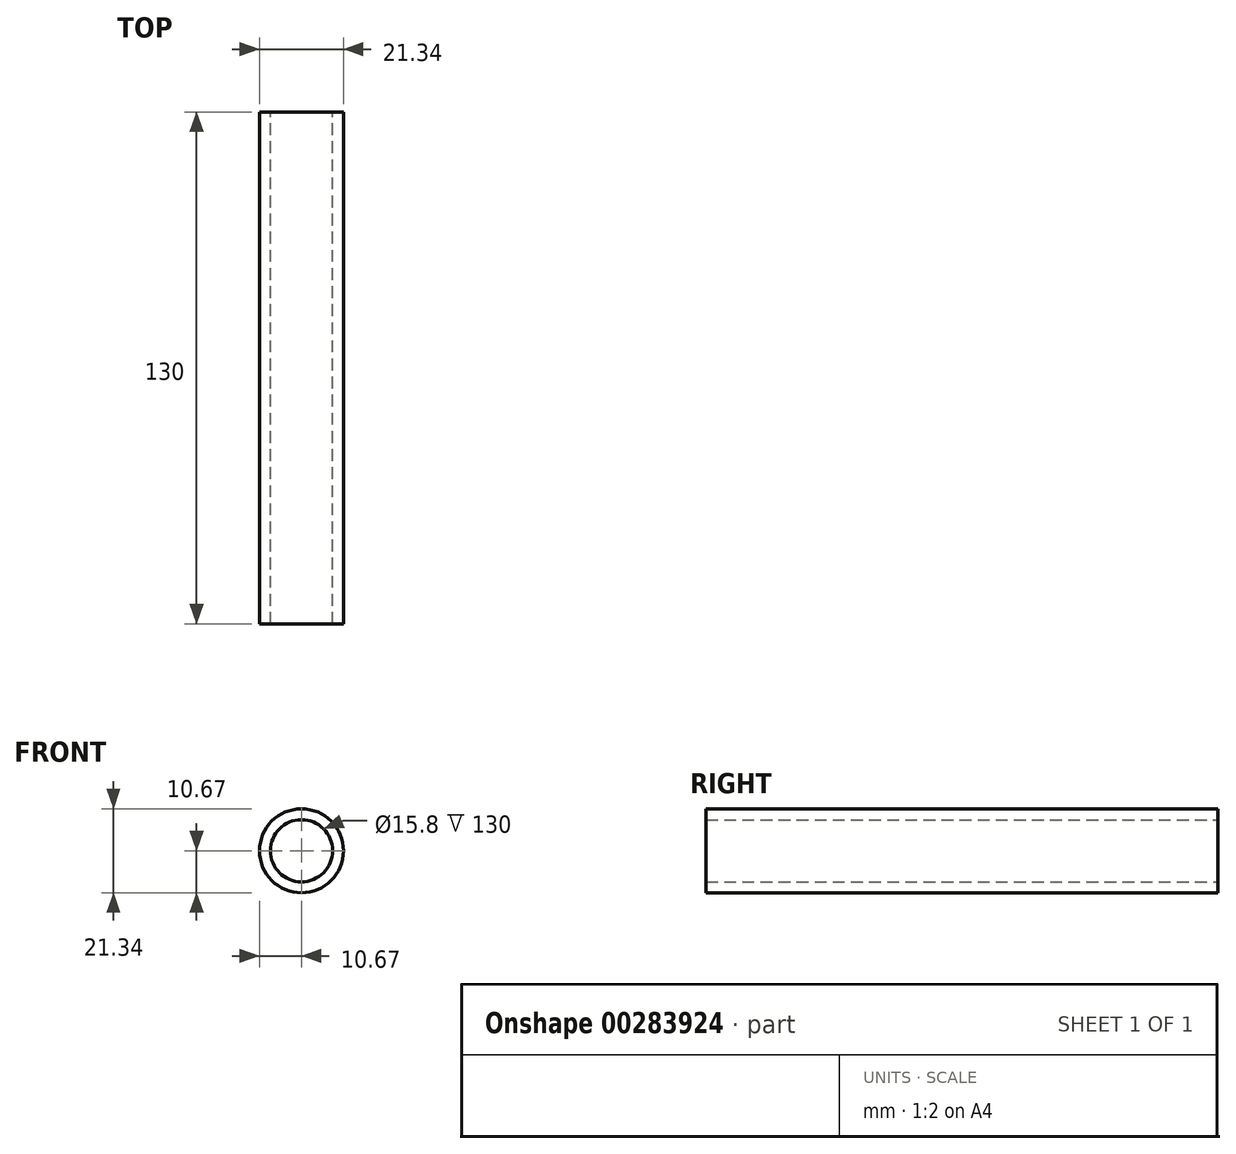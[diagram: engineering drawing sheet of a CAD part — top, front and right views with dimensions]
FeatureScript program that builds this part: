
annotation { "Feature Type Name" : "Feature", "Feature Type Description" : "" }
export const myFeature = defineFeature(function(context is Context, id is Id, definition is map)
    precondition{}
    {
        {
            var Q0;
            Q0=qCreatedBy(makeId("Front.planeOp"),FACE);
            var sketch = newSketch(context, id + "F0", { "sketchPlane" : qUnion([Q0])});
            skCircle(sketch, "E0", {"center": v(0, 0) * mm, "radius": 7.9 * mm});
            skCircle(sketch, "E1", {"center": v(0, 0) * mm, "radius": 10.67 * mm});
            skSolve(sketch);
        }
        {
            var Q0;
            Q0=qSketchRegion(id+"F0",true);
            extrude(context, id + "F1", {"entities" : qUnion([Q0]), "endBound" : BoundingType.SYMMETRIC, "depth" : 130 * mm});
        }
    });
